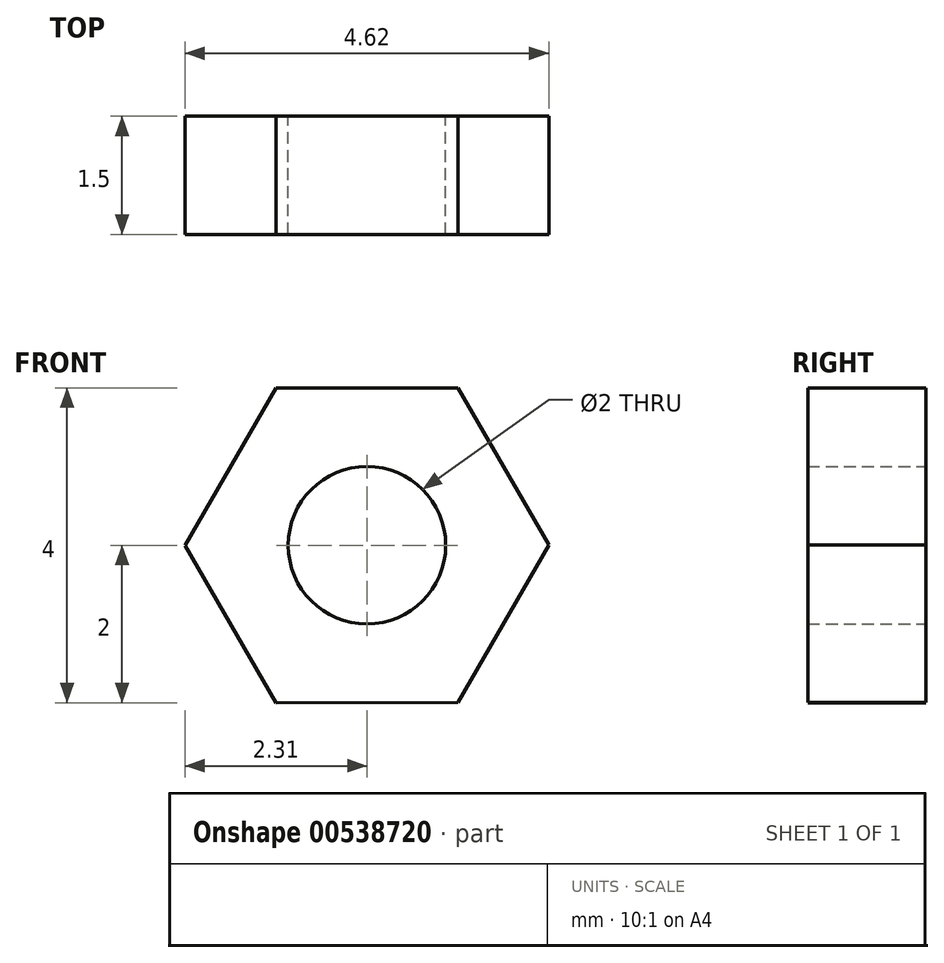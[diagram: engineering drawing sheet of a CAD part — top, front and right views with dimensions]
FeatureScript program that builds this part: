
annotation { "Feature Type Name" : "Feature", "Feature Type Description" : "" }
export const myFeature = defineFeature(function(context is Context, id is Id, definition is map)
    precondition{}
    {
        {
            var Q0;
            Q0=qCreatedBy(makeId("Front.planeOp"),FACE);
            var sketch = newSketch(context, id + "F0", { "sketchPlane" : qUnion([Q0])});
            skCircle(sketch, "E0.cCircle", {"center": v(0, 0) * mm, "radius": 2 * mm, "construction": true});
            skLineSegment(sketch, "E0.0", {"start": v(2.3, 0) * mm, "end": v(1.16, -2) * mm});
            skLineSegment(sketch, "E0.1", {"start": v(1.16, -2) * mm, "end": v(-1.15, -2) * mm});
            skLineSegment(sketch, "E0.2", {"start": v(-1.15, -2) * mm, "end": v(-2.3, 0) * mm});
            skLineSegment(sketch, "E0.3", {"start": v(-2.3, 0) * mm, "end": v(-1.16, 2) * mm});
            skLineSegment(sketch, "E0.4", {"start": v(-1.16, 2) * mm, "end": v(1.15, 2) * mm});
            skLineSegment(sketch, "E0.5", {"start": v(1.15, 2) * mm, "end": v(2.3, 0) * mm});
            skPoint(sketch, "E0.0.midPoint", {"position": v(1.73, -1) * mm});
            skCircle(sketch, "E1", {"center": v(0, 0) * mm, "radius": 1 * mm});
            skSolve(sketch);
        }
        {
            var Q0;
            Q0=makeQuery(id+"F0.imprint","IMPRINT",FACE,{"disambiguationData":[TD([[makeQuery(id+"F0.imprint","IMPRINT",EDGE,{"derivedFrom":sQuery(id+"F0.wireOp",EDGE,"E0.0")}),-1.0]])]});
            extrude(context, id + "F1", {"entities" : qUnion([Q0]), "depth" : 1.5 * mm, "offsetDistance" : 25 * mm});
        }
    });
